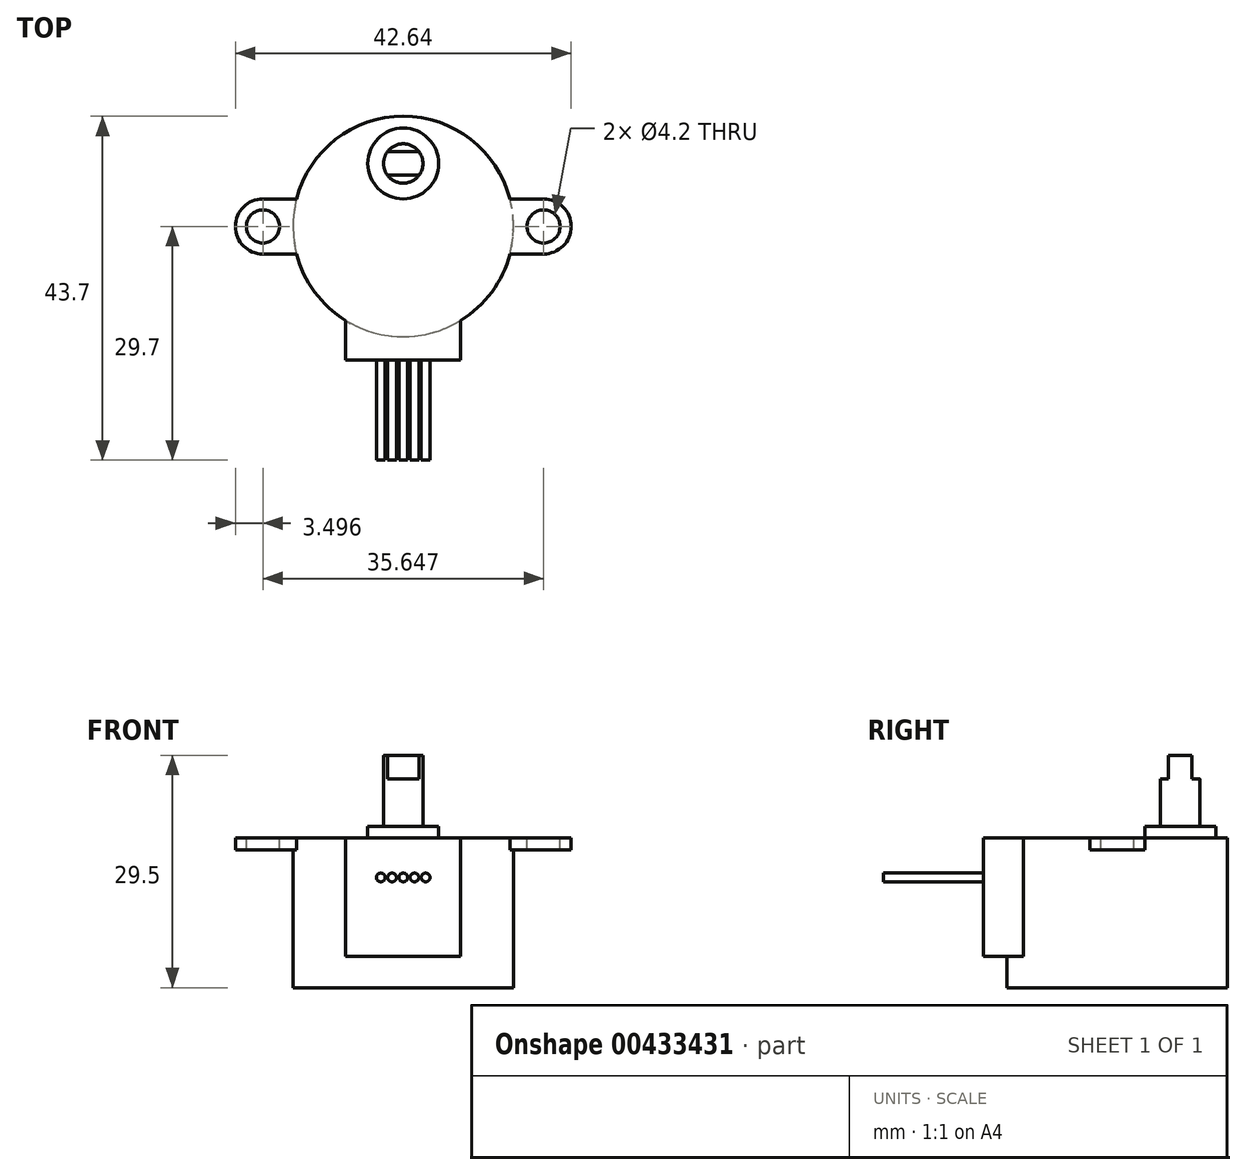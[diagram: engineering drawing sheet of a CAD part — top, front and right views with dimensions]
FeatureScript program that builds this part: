
annotation { "Feature Type Name" : "Feature", "Feature Type Description" : "" }
export const myFeature = defineFeature(function(context is Context, id is Id, definition is map)
    precondition{}
    {
        {
            var Q0;
            Q0=qCreatedBy(makeId("Top.planeOp"),FACE);
            var sketch = newSketch(context, id + "F0", { "sketchPlane" : qUnion([Q0])});
            skArc(sketch, "E0", {"start": v(7.3, -19.95) * mm, "mid": v(0, 6) * mm, "end": v(-7.3, -19.95) * mm});
            skLineSegment(sketch, "E1", {"start": v(0, 0) * mm, "end": v(0, -8) * mm, "construction": true});
            skLineSegment(sketch, "E2", {"start": v(-7.3, -25) * mm, "end": v(-7.3, -19.95) * mm});
            skLineSegment(sketch, "E3.MirrorCS", {"start": v(7.3, -25) * mm, "end": v(7.3, -19.95) * mm});
            skLineSegment(sketch, "E4", {"start": v(-7.3, -25) * mm, "end": v(7.3, -25) * mm});
            skArc(sketch, "E5", {"start": v(7.3, -19.95) * mm, "mid": v(0, -22) * mm, "end": v(-7.3, -19.95) * mm, "construction": true});
            skSolve(sketch);
        }
        {
            var Q0;
            Q0 = qSketchRegion(id + "F0", true);
            extrude(context, id + "F1", {"entities" : qUnion([Q0]), "oppositeDirection" : true, "depth" : 15 * mm});
        }
        {
            var Q0;
            Q0=makeQuery(id+"F1.opExtrude","CAP_FACE",FACE,{"disambiguationData":[OSD([sQuery(id+"F0.wireOp",EDGE,"E0"),sQuery(id+"F0.wireOp",EDGE,"E2"),sQuery(id+"F0.wireOp",EDGE,"E3.MirrorCS"),sQuery(id+"F0.wireOp",EDGE,"E4")])],"isStart":false});
            var sketch = newSketch(context, id + "F2", { "sketchPlane" : qUnion([Q0])});
            skCircle(sketch, "E6", {"center": v(0, 8) * mm, "radius": 14 * mm});
            skSolve(sketch);
        }
        {
            var Q0;
            Q0 = qSketchRegion(id + "F2", true);
            extrude(context, id + "F3", {"entities" : qUnion([Q0]), "operationType" : NewBodyOperationType.ADD, "depth" : 4 * mm});
        }
        {
            var Q0;
            Q0=qCreatedBy(makeId("Top.planeOp"),FACE);
            var sketch = newSketch(context, id + "F4", { "sketchPlane" : qUnion([Q0])});
            skLineSegment(sketch, "E7", {"start": v(-17.82, -8) * mm, "end": v(17.82, -8) * mm, "construction": true});
            skPoint(sketch, "E8", {"position": v(0, -8) * mm});
            skPoint(sketch, "E8.positionSnap0", {"position": v(0, -8) * mm});
            skLineSegment(sketch, "E9", {"start": v(0, -8) * mm, "end": v(0, 0) * mm, "construction": true});
            skArc(sketch, "E10.0.startCap", {"start": v(-17.82, -11.5) * mm, "mid": v(-21.32, -8) * mm, "end": v(-17.82, -4.5) * mm});
            skArc(sketch, "E10.0.endCap", {"start": v(17.82, -4.5) * mm, "mid": v(21.32, -8) * mm, "end": v(17.82, -11.5) * mm});
            skLineSegment(sketch, "E10.0.left", {"start": v(-17.82, -4.5) * mm, "end": v(17.82, -4.5) * mm});
            skLineSegment(sketch, "E10.0.right", {"start": v(-17.82, -11.5) * mm, "end": v(17.82, -11.5) * mm});
            skCircle(sketch, "E11", {"center": v(17.82, -8) * mm, "radius": 2.1 * mm});
            skCircle(sketch, "E12", {"center": v(-17.82, -8) * mm, "radius": 2.1 * mm});
            skSolve(sketch);
        }
        {
            var Q0;
            Q0 = qSketchRegion(id + "F4", true);
            extrude(context, id + "F5", {"entities" : qUnion([Q0]), "operationType" : NewBodyOperationType.ADD, "oppositeDirection" : true, "depth" : 1.5 * mm});
        }
        {
            var Q0;
            Q0=qCreatedBy(makeId("Top.planeOp"),FACE);
            cPlane(context, id + "F6", {"entities" : qUnion([Q0]), "cplaneType" : CPlaneType.OFFSET, "offset" : 5 * mm, "oppositeDirection" : true, "width" : 152.4 * mm, "height" : 152.4 * mm});
        }
        {
            var Q0;
            Q0=makeQuery(id+"F1.opExtrude","SWEPT_FACE",FACE,{"disambiguationData":[OSD([sQuery(id+"F0.wireOp",EDGE,"E4")])]});
            var sketch = newSketch(context, id + "F7", { "sketchPlane" : qUnion([Q0])});
            skPoint(sketch, "E13", {"position": v(-2.84, -5) * mm});
            skCircle(sketch, "E14", {"center": v(-2.84, -5) * mm, "radius": 0.56 * mm});
            skCircle(sketch, "E15.1.0.0", {"center": v(-1.42, -5) * mm, "radius": 0.56 * mm});
            skCircle(sketch, "E15.2.0.0", {"center": v(0, -5) * mm, "radius": 0.56 * mm});
            skCircle(sketch, "E15.3.0.0", {"center": v(1.42, -5) * mm, "radius": 0.56 * mm});
            skCircle(sketch, "E15.4.0.0", {"center": v(2.84, -5) * mm, "radius": 0.56 * mm});
            skLineSegment(sketch, "E15.direction1", {"start": v(-2.84, -5) * mm, "end": v(-1.42, -5) * mm, "construction": true});
            skSolve(sketch);
        }
        {
            var Q0;
            Q0 = qSketchRegion(id + "F7", true);
            extrude(context, id + "F8", {"entities" : qUnion([Q0]), "operationType" : NewBodyOperationType.ADD, "depth" : 12.7 * mm});
        }
        {
            var Q0;
            Q0=qCreatedBy(makeId("Right.planeOp"),FACE);
            var sketch = newSketch(context, id + "F9", { "sketchPlane" : qUnion([Q0])});
            skLineSegment(sketch, "E16", {"start": v(0, 0) * mm, "end": v(0, 7.5) * mm});
            skLineSegment(sketch, "E17", {"start": v(4.5, 0) * mm, "end": v(0, 0) * mm});
            skLineSegment(sketch, "E18", {"start": v(4.5, 0) * mm, "end": v(4.5, 1.5) * mm});
            skLineSegment(sketch, "E19", {"start": v(4.5, 1.5) * mm, "end": v(2.5, 1.5) * mm});
            skLineSegment(sketch, "E20", {"start": v(2.5, 1.5) * mm, "end": v(2.5, 7.5) * mm});
            skLineSegment(sketch, "E21", {"start": v(1.5, 7.5) * mm, "end": v(1.5, 10.5) * mm, "construction": true});
            skLineSegment(sketch, "E22.MirrorCS", {"start": v(-4.5, 0) * mm, "end": v(-4.5, 1.5) * mm, "construction": true});
            skLineSegment(sketch, "E23.MirrorCS", {"start": v(-2.5, 1.5) * mm, "end": v(-2.5, 7.5) * mm, "construction": true});
            skLineSegment(sketch, "E24.MirrorCS", {"start": v(-1.5, 7.5) * mm, "end": v(-1.5, 10.5) * mm, "construction": true});
            skLineSegment(sketch, "E25", {"start": v(2.5, 7.5) * mm, "end": v(0, 7.5) * mm});
            skPoint(sketch, "E26.orphan", {"position": v(0, 7.5) * mm});
            skSolve(sketch);
        }
        {
            var Q0;
            Q0 = qSketchRegion(id + "F9", true);
            var Q1;
            Q1=sQuery(id+"F9.wireOp",EDGE,"E16");
            revolve(context, id + "F10", {"operationType" : NewBodyOperationType.ADD, "entities" : qUnion([Q0]), "axis" : qUnion([Q1]), "revolveType" : RevolveType.FULL});
        }
        {
            var Q0;
            Q0=makeQuery(id+"F10.opRevolve","SWEPT_FACE",FACE,{"disambiguationData":[OSD([sQuery(id+"F9.wireOp",EDGE,"E25")])]});
            cPlane(context, id + "F11", {"entities" : qUnion([Q0]), "cplaneType" : CPlaneType.OFFSET, "offset" : 3 * mm, "width" : 152.4 * mm, "height" : 152.4 * mm});
        }
        {
            var Q0;
            Q0=qCreatedBy(id+"F11.planeOp",FACE);
            var sketch = newSketch(context, id + "F12", { "sketchPlane" : qUnion([Q0])});
            skArc(sketch, "E27", {"start": v(-2, 1.5) * mm, "mid": v(-2.5, 0) * mm, "end": v(-2, -1.5) * mm});
            skLineSegment(sketch, "E28", {"start": v(-2.5, 0) * mm, "end": v(2.5, 0) * mm, "construction": true});
            skLineSegment(sketch, "E29", {"start": v(-2, 1.5) * mm, "end": v(2, 1.5) * mm});
            skLineSegment(sketch, "E30.MirrorCS", {"start": v(-2, -1.5) * mm, "end": v(2, -1.5) * mm});
            skArc(sketch, "E31.trimOffspring", {"start": v(2, -1.5) * mm, "mid": v(2.5, 0) * mm, "end": v(2, 1.5) * mm});
            skSolve(sketch);
        }
        {
            var Q0;
            Q0 = qSketchRegion(id + "F12", true);
            extrude(context, id + "F13", {"entities" : qUnion([Q0]), "operationType" : NewBodyOperationType.ADD, "endBound" : BoundingType.UP_TO_NEXT, "oppositeDirection" : true, "depth" : 25.4 * mm});
        }
    });
